# Revit family: Excitech_Delmatic_LightingControlModule_163A1-DaliPresenceDetector
name_source: partatom
category: Electrical Equipment
revit_build: Autodesk Revit 2013 (Build: 20130531_2115(x64)
units: mm (PartAtom-declared; Revit-internal decimal feet)

## types (1)
- Excitech_Delmatic_LightingControlModule_163A1-DaliPresenceDetector
    AssetType = Fixed
    BIMObjectName = Excitech_Delmatic_LightingControlModule_DaliPresenceDetector_163A1
    Category = Ac-45-65-47
    Color = RAL 9002
    Constituents = Modular unit comprises single-fix sensor with spring-clip mountings.
    Default Elevation = 0 mm  [stored 0 ft]
    Description = The Dali Multisensor combines presence and absence detection with daylight linking within an ultra-low profile and compact diameter unit.  The multisensor is fully software-configurable and all operating parameters including time-out period, daylight thresholds, etc are configured through graphical Lightscape software.
    DurationUnit = year
    ExpectedLife = 20
    Features = Ultra low-profile sensor.
Ultra-small diameter bezel.
Fully-software configurable for time-out period and daylight level thresholds.
Software configurable presence or absence detection mode.
Integral infra-red receiver for remote control. 
Connect to Dali Plug-in Module or direct to Dali buswire.
    Finish = Moulded enclosure
    IfcExportAs = IfcElectricDistributionPoint
    IfcExportType = NOTDEFINED
    IfcTypeObject = IfcBuildingElementProxy
    MCB Rating = 10 A
    Mains Type = Single phase
    Manufacturer = Delmatic Lighting Management
    ManufacturerURL = www.delmatic.com/contact
    Material = Flame retardant ABS enclosure
    Model = 163A1, Dali presence detector
    ModelNumber = 164A1
    ModelReference = Multisensor 164A1
    MovementSensingType = Passive Infra Red
    NBSDescription = Hard wired general lighting system
    NBSReference = 70-80-35/110
    Name = Dali Multisensor
    NominalHeight = 35 mm
    NominalLength = 50 mm  [stored 0.164042 ft]
    NominalWidth = 50 mm  [stored 0.164042 ft]
    ProductInformation = http://www.delmatic.com
    Revision = 3
    Shape = Rectangular
    Size = Compact
    SustainabilityPerformance = The module is designed to maximise sustainability through the use of modular electronics which enable products to be upgraded with 90% of the unit being re-used.
    TimeConstant = Software Configurable
    URL = http://www.delmatic.com
    Uniclass1 = G543
    Uniclass2 = Ac-45-65-47
    UnitMaterial = ABS Plastic
    Version = 4
    Voltage = 18
    WarrantyDescription = Warranty allows for free of charge factory repair or replacement of any parts proving to be faulty provided they have been installed and operated correctly.
    WarrantyDurationLabor = 1
    WarrantyDurationParts = 8
    WarrantyDurationUnit = year
    Wattage = 70mW

note: [stored X ft] marks values corroborated as IEEE doubles in the binary element streams (Revit-internal decimal feet)

## geometry (parser evidence)
native form markers: Blend x4, Sweep x4
no freeform markers — native parametric forms only
